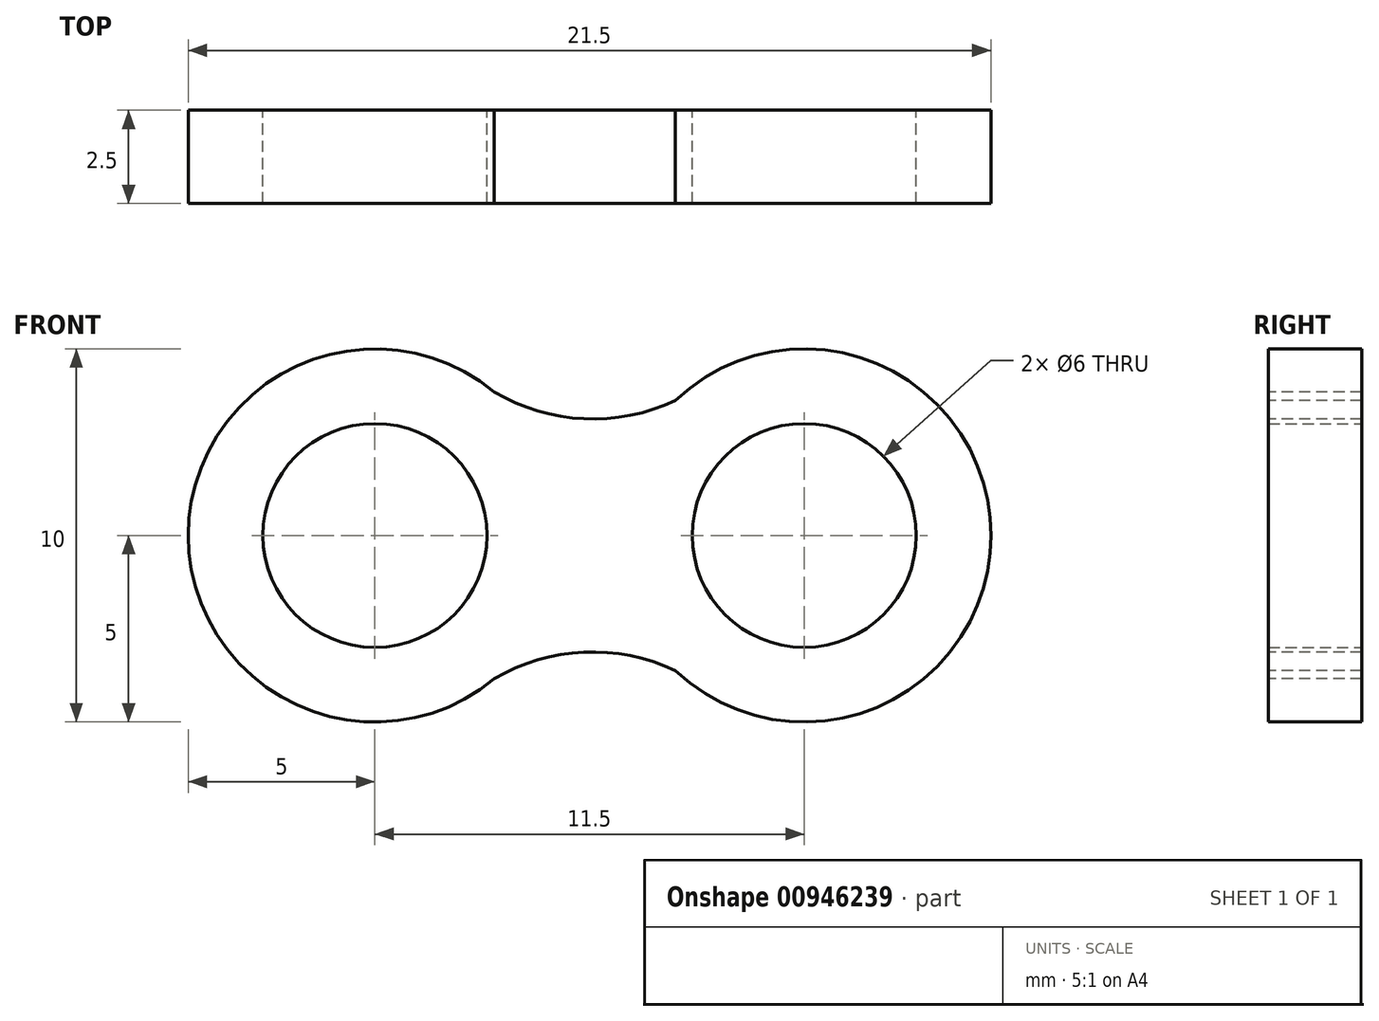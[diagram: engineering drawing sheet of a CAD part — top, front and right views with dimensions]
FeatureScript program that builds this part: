
annotation { "Feature Type Name" : "Feature", "Feature Type Description" : "" }
export const myFeature = defineFeature(function(context is Context, id is Id, definition is map)
    precondition{}
    {
        {
            var Q0;
            Q0=qCreatedBy(makeId("Front.planeOp"),FACE);
            var sketch = newSketch(context, id + "F0", { "sketchPlane" : qUnion([Q0])});
            skCircle(sketch, "E0", {"center": v(0, 0) * mm, "radius": 5 * mm});
            skCircle(sketch, "E1", {"center": v(0, 0) * mm, "radius": 3 * mm});
            skSolve(sketch);
        }
        {
            var Q0;
            Q0=makeQuery(id+"F0.imprint","IMPRINT",FACE,{"disambiguationData":[TD([[makeQuery(id+"F0.imprint","IMPRINT",EDGE,{"derivedFrom":sQuery(id+"F0.wireOp",EDGE,"E0")}),1.0]])]});
            extrude(context, id + "F1", {"entities" : qUnion([Q0]), "depth" : 2.5 * mm, "offsetDistance" : 25.4 * mm});
        }
        {
            var Q0;
            Q0=qCreatedBy(makeId("Front.planeOp"),FACE);
            var sketch = newSketch(context, id + "F2", { "sketchPlane" : qUnion([Q0])});
            skCircle(sketch, "E2", {"center": v(11.5, 0) * mm, "radius": 5 * mm});
            skCircle(sketch, "E3", {"center": v(11.5, 0) * mm, "radius": 3 * mm});
            skSolve(sketch);
        }
        {
            var Q0;
            Q0=makeQuery(id+"F2.imprint","IMPRINT",FACE,{"disambiguationData":[TD([[makeQuery(id+"F2.imprint","IMPRINT",EDGE,{"derivedFrom":sQuery(id+"F2.wireOp",EDGE,"E2")}),1.0]])]});
            extrude(context, id + "F3", {"entities" : qUnion([Q0]), "depth" : 2.5 * mm, "offsetDistance" : 25.4 * mm});
        }
        {
            var Q0;
            Q0=makeQuery(id+"F1.opExtrude","CAP_FACE",FACE,{"disambiguationData":[OSD([sQuery(id+"F0.wireOp",EDGE,"E0"),sQuery(id+"F0.wireOp",EDGE,"E1")])],"isStart":false});
            var sketch = newSketch(context, id + "F4", { "sketchPlane" : qUnion([Q0])});
            skArc(sketch, "E4", {"start": v(3.2, 3.84) * mm, "mid": v(5, 0) * mm, "end": v(3.2, -3.84) * mm});
            skArc(sketch, "E5", {"start": v(3.2, 3.84) * mm, "mid": v(5.84, 3.12) * mm, "end": v(8.47, 3.84) * mm});
            skArc(sketch, "E6.MirrorCS", {"start": v(3.2, -3.84) * mm, "mid": v(5.84, -3.12) * mm, "end": v(8.47, -3.84) * mm});
            skPoint(sketch, "E7", {"position": v(11.5, 0) * mm});
            skArc(sketch, "E8", {"start": v(8.47, 3.84) * mm, "mid": v(6.6, 0) * mm, "end": v(8.47, -3.84) * mm});
            skLineSegment(sketch, "E9", {"start": v(8.47, 3.84) * mm, "end": v(8.47, -3.84) * mm, "construction": true});
            skLineSegment(sketch, "E10", {"start": v(3.2, 3.84) * mm, "end": v(3.2, -3.84) * mm, "construction": true});
            skLineSegment(sketch, "E11", {"start": v(3.2, -3.84) * mm, "end": v(8.47, -3.84) * mm, "construction": true});
            skSolve(sketch);
        }
        {
            var Q0;
            Q0 = qSketchRegion(id + "F4", true);
            extrude(context, id + "F5", {"entities" : qUnion([Q0]), "operationType" : NewBodyOperationType.ADD, "oppositeDirection" : true, "depth" : 2.5 * mm, "offsetDistance" : 25.4 * mm});
        }
    });
